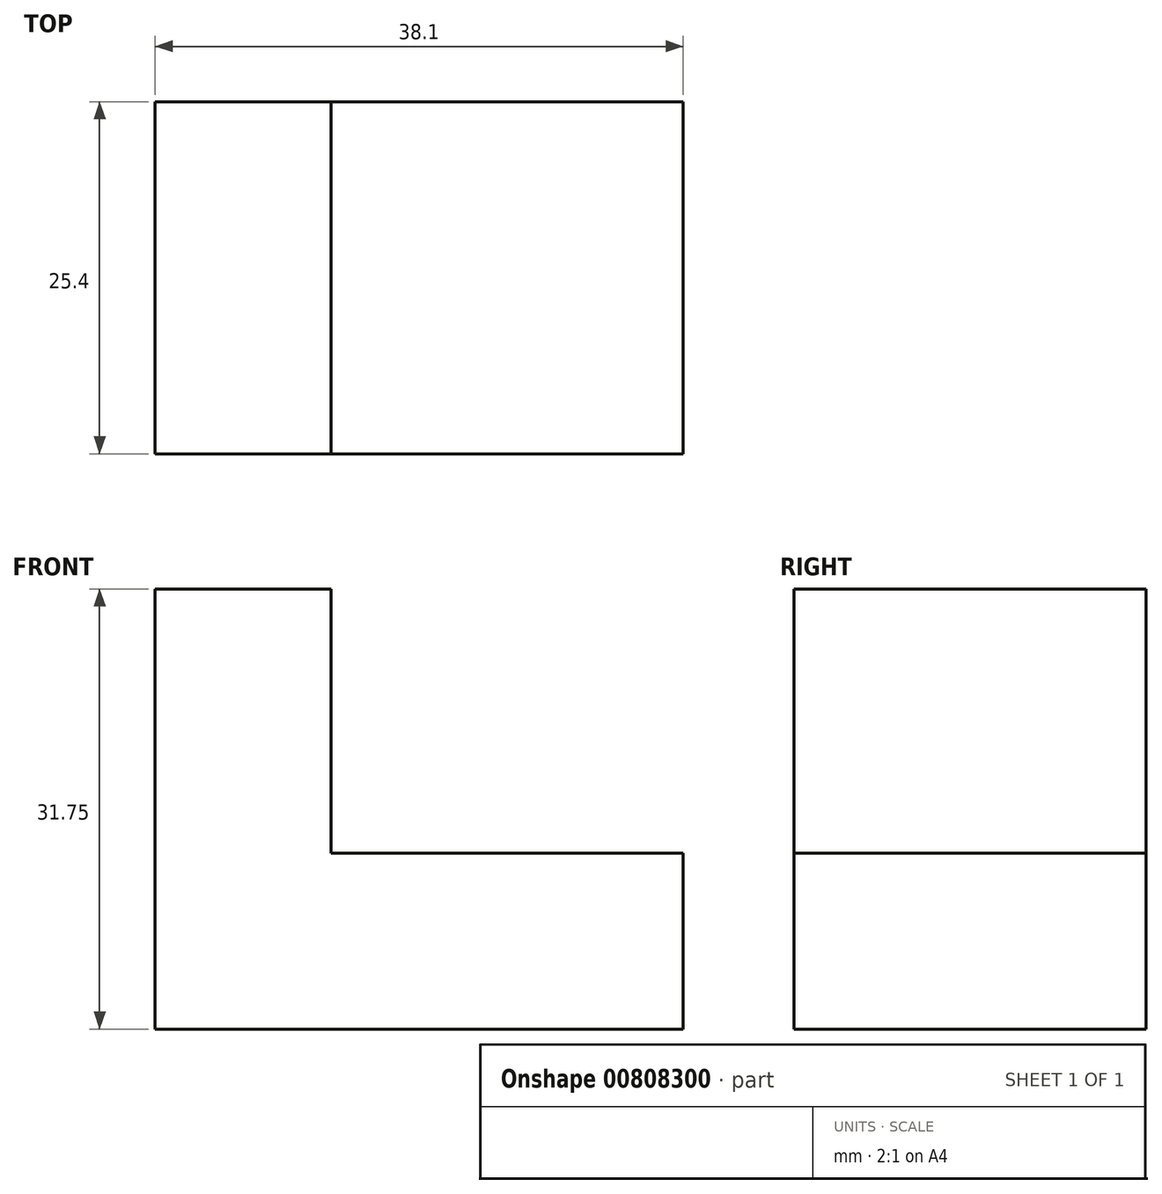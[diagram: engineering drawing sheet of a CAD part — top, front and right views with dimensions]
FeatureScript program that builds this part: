
annotation { "Feature Type Name" : "Feature", "Feature Type Description" : "" }
export const myFeature = defineFeature(function(context is Context, id is Id, definition is map)
    precondition{}
    {
        {
            var Q0;
            Q0=qCreatedBy(makeId("Front.planeOp"),FACE);
            var sketch = newSketch(context, id + "F0", { "sketchPlane" : qUnion([Q0])});
            skLineSegment(sketch, "E0", {"start": v(0, 0) * mm, "end": v(0, 11.2) * mm});
            skLineSegment(sketch, "E1", {"start": v(0, 0) * mm, "end": v(0, 31.75) * mm});
            skLineSegment(sketch, "E2", {"start": v(0, 31.75) * mm, "end": v(12.7, 31.75) * mm});
            skLineSegment(sketch, "E3", {"start": v(12.7, 31.75) * mm, "end": v(12.7, 12.7) * mm});
            skLineSegment(sketch, "E4", {"start": v(12.7, 12.7) * mm, "end": v(38.1, 12.7) * mm});
            skLineSegment(sketch, "E5", {"start": v(38.1, 12.7) * mm, "end": v(38.1, 0) * mm});
            skLineSegment(sketch, "E6", {"start": v(38.1, 0) * mm, "end": v(0, 0) * mm});
            skSolve(sketch);
        }
        {
            var Q0;
            Q0 = qSketchRegion(id + "F0", true);
            extrude(context, id + "F1", {"entities" : qUnion([Q0]), "depth" : 25.4 * mm, "offsetDistance" : 25.4 * mm});
        }
    });
